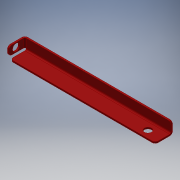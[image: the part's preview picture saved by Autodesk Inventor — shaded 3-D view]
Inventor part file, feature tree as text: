
AUTODESK INVENTOR PART (.ipt)
format: ipt  version: 2018 (Build 220112000, 112)  size: 159,744 bytes
history: native  units: mm
features: other x11, sketch x5, hole x2
ambient origin geometry x8: Origin, YZ Plane, XZ Plane, XY Plane, X Axis, Y Axis, Z Axis, Center Point
bodies: Body1 (feature_tree)
feature tree (18):
  other  "Faccia4"
  other  "Flangia9"
  other  "Flangia10"
  hole  "Foro7"  [1 undecoded]
  other  "Arrotondamento angolo7"
  hole  "Foro8"  [1 undecoded]
  sketch  "Schizzo9"
  other  "Piano6"
  sketch  "Schizzo19"
  other  "Piano13"
  other  "Piega (Bend)9"
  other  "Angolo9"
  sketch  "Schizzo20"
  other  "Piano14"
  other  "Piega (Bend)10"
  other  "Angolo10"
  sketch  "Schizzo21"
  sketch  "Schizzo22"
note: 2 required parameter values undecoded (feature->parameter linkage not recoverable at this tier; creation-order binding heuristic only, values carry confidence <= 0.55)
